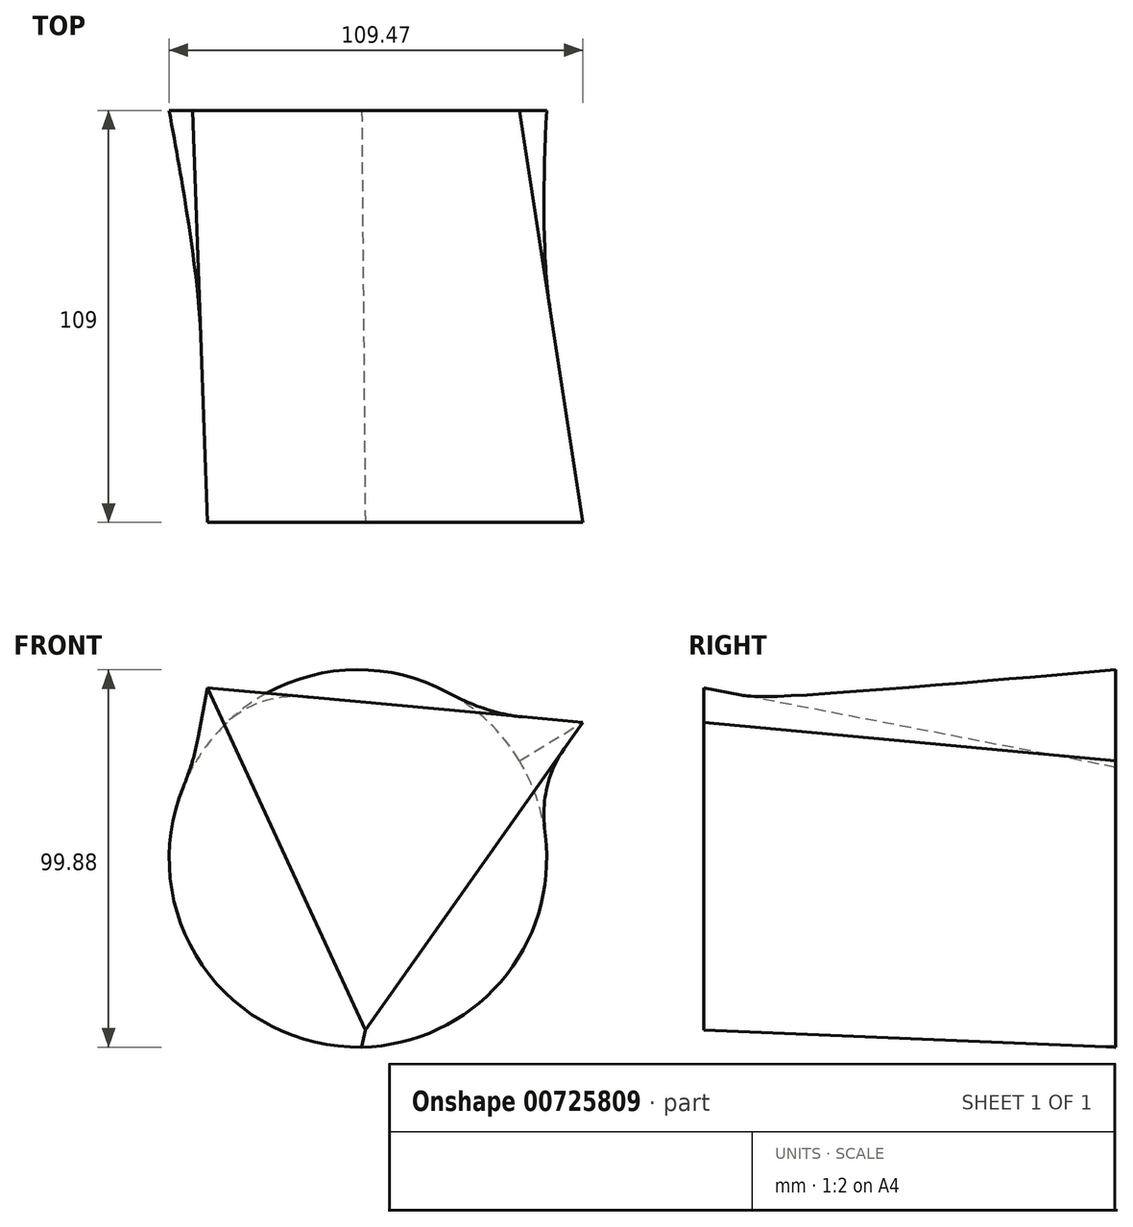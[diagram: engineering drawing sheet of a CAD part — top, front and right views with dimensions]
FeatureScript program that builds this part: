
annotation { "Feature Type Name" : "Feature", "Feature Type Description" : "" }
export const myFeature = defineFeature(function(context is Context, id is Id, definition is map)
    precondition{}
    {
        {
            var Q0;
            Q0=qCreatedBy(makeId("Front.planeOp"),FACE);
            cPlane(context, id + "F0", {"entities" : qUnion([Q0]), "cplaneType" : CPlaneType.OFFSET, "offset" : 59 * mm, "width" : 152.4 * mm, "height" : 152.4 * mm});
        }
        {
            var Q0;
            Q0=qCreatedBy(id+"F0.planeOp",FACE);
            cPlane(context, id + "F1", {"entities" : qUnion([Q0]), "cplaneType" : CPlaneType.OFFSET, "offset" : 109 * mm, "width" : 150 * mm, "height" : 150 * mm});
        }
        {
            var Q0;
            Q0=qCreatedBy(id+"F0.planeOp",FACE);
            var sketch = newSketch(context, id + "F2", { "sketchPlane" : qUnion([Q0])});
            skCircle(sketch, "E0", {"center": v(-22.02, 0) * mm, "radius": 49.94 * mm});
            skSolve(sketch);
        }
        {
            var Q0;
            Q0=qCreatedBy(id+"F1.planeOp",FACE);
            var sketch = newSketch(context, id + "F3", { "sketchPlane" : qUnion([Q0])});
            skCircle(sketch, "E1.cCircle", {"center": v(-14.8, 11.9) * mm, "radius": 28.79 * mm, "construction": true});
            skLineSegment(sketch, "E1.0", {"start": v(37.5, 36) * mm, "end": v(-20.08, -45.43) * mm});
            skLineSegment(sketch, "E1.1", {"start": v(-20.08, -45.43) * mm, "end": v(-61.8, 45.14) * mm});
            skLineSegment(sketch, "E1.2", {"start": v(-61.8, 45.14) * mm, "end": v(37.5, 36) * mm});
            skPoint(sketch, "E1.0.midPoint", {"position": v(8.7, -4.72) * mm});
            skSolve(sketch);
        }
        {
            var Q0;
            Q0=makeQuery(id+"F2.imprint","IMPRINT",FACE,{"disambiguationData":[TD([[makeQuery(id+"F2.imprint","IMPRINT",EDGE,{"derivedFrom":sQuery(id+"F2.wireOp",EDGE,"E0")}),1.0]])]});
            var Q1;
            Q1=makeQuery(id+"F3.imprint","IMPRINT",FACE,{"disambiguationData":[TD([[makeQuery(id+"F3.imprint","IMPRINT",EDGE,{"derivedFrom":sQuery(id+"F3.wireOp",EDGE,"E1.0")}),-1.0]])]});
            loft(context, id + "F4", {"sheetProfilesArray" : [{ "sheetProfileEntities" : qUnion([Q0]) }, { "sheetProfileEntities" : qUnion([Q1]) }]});
        }
    });
